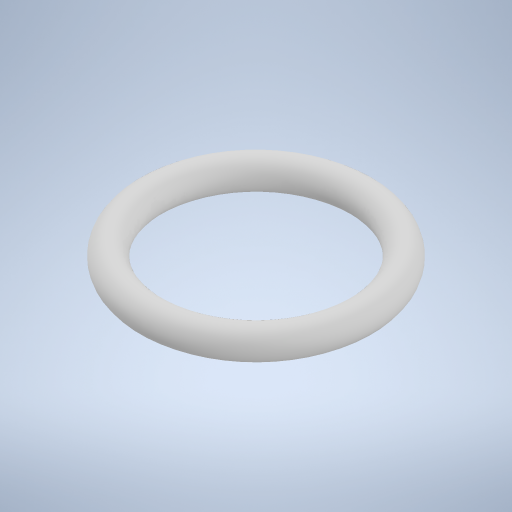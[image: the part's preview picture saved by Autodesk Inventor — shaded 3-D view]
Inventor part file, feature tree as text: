
AUTODESK INVENTOR PART (.ipt)
format: ipt  version: 2023 (Build 270158000, 158)  size: 268,288 bytes
history: native  units: in
note: dims shown in document units (in); Inventor stores cm internally (conversion verified against a paired STEP export)
features: sketch x2, sweep x1
ambient origin geometry x8: Origin, YZ Plane, XZ Plane, XY Plane, X Axis, Y Axis, Z Axis, Center Point
bodies: Solid1 (feature_tree)
feature tree (3):
  sweep  "Sweep1"
  sketch  "Sketch1"  dims[d0=1.3125in d3=0.1875in]
  sketch  "Sketch2"  dims[d4=0.0in d5=0.0in]
